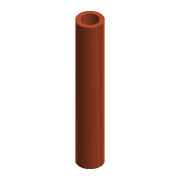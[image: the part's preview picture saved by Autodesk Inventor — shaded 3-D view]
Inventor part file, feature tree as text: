
AUTODESK INVENTOR PART (.ipt)
format: ipt  version: 2016 SP2 (Build 200236200, 236)  size: 82,944 bytes
history: native  units: mm
features: extrude x1, sketch x1
ambient origin geometry x8: Origin, YZ Plane, XZ Plane, XY Plane, X Axis, Y Axis, Z Axis, Center Point
bodies: Body1 (feature_tree)
feature tree (2):
  extrude  "Extrusion3"  Depth=40.0mm
  sketch  "Sketch1"  dims[d4=6.0mm d5=4.0mm d6=40.0mm d7=0.0mm]
